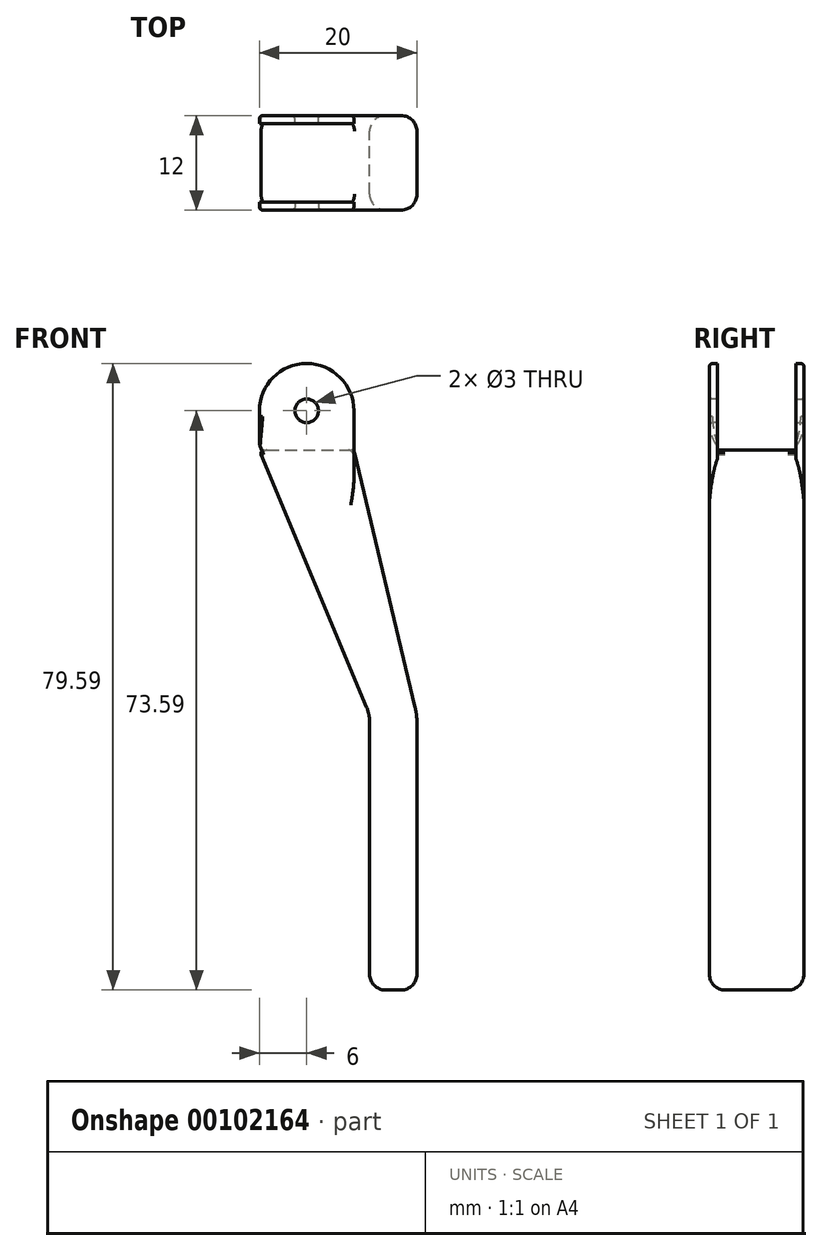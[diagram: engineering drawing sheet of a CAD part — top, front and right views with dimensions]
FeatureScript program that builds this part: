
annotation { "Feature Type Name" : "Feature", "Feature Type Description" : "" }
export const myFeature = defineFeature(function(context is Context, id is Id, definition is map)
    precondition{}
    {
        {
            var Q0;
            Q0=qCreatedBy(makeId("Front.planeOp"),FACE);
            var sketch = newSketch(context, id + "F0", { "sketchPlane" : qUnion([Q0])});
            skLineSegment(sketch, "E0", {"start": v(0, 0) * mm, "end": v(12, 0) * mm});
            skLineSegment(sketch, "E1", {"start": v(12, 0) * mm, "end": v(20, -33.59) * mm});
            skLineSegment(sketch, "E2", {"start": v(20, -33.59) * mm, "end": v(20, -68.59) * mm});
            skLineSegment(sketch, "E3", {"start": v(20, -68.59) * mm, "end": v(14, -68.59) * mm});
            skLineSegment(sketch, "E4", {"start": v(14, -68.59) * mm, "end": v(14, -33.59) * mm});
            skLineSegment(sketch, "E5", {"start": v(14, -33.59) * mm, "end": v(0, 0) * mm});
            skLineSegment(sketch, "E6", {"start": v(14, -33.59) * mm, "end": v(20, -33.59) * mm});
            skSolve(sketch);
        }
        {
            var Q0;
            Q0 = qSketchRegion(id + "F0", true);
            extrude(context, id + "F1", {"entities" : qUnion([Q0]), "depth" : 6 * mm, "hasSecondDirection" : true, "secondDirectionOppositeDirection" : true, "secondDirectionDepth" : 6 * mm});
        }
        {
            var Q0;
            Q0 = qSketchRegion(id + "F0", true);
            extrude(context, id + "F2", {"entities" : qUnion([Q0]), "operationType" : NewBodyOperationType.ADD, "depth" : 6 * mm, "hasSecondDirection" : true, "secondDirectionOppositeDirection" : true, "secondDirectionDepth" : 6 * mm});
        }
        {
            var Q0;
            Q0=makeQuery(id+"F1.opExtrude","CAP_FACE",FACE,{"disambiguationData":[OSD([sQuery(id+"F0.wireOp",EDGE,"E0"),sQuery(id+"F0.wireOp",EDGE,"E1"),sQuery(id+"F0.wireOp",EDGE,"E2"),sQuery(id+"F0.wireOp",EDGE,"E3"),sQuery(id+"F0.wireOp",EDGE,"E4"),sQuery(id+"F0.wireOp",EDGE,"E5")])],"isStart":false});
            var sketch = newSketch(context, id + "F3", { "sketchPlane" : qUnion([Q0])});
            skLineSegment(sketch, "E7.bottom", {"start": v(0, 0) * mm, "end": v(12, 0) * mm});
            skLineSegment(sketch, "E7.top", {"start": v(0, 5) * mm, "end": v(12, 5) * mm});
            skLineSegment(sketch, "E7.left", {"start": v(0, 0) * mm, "end": v(0, 5) * mm});
            skLineSegment(sketch, "E7.right", {"start": v(12, 0) * mm, "end": v(12, 5) * mm});
            skArc(sketch, "E8", {"start": v(12, 5) * mm, "mid": v(6, 11) * mm, "end": v(0, 5) * mm});
            skCircle(sketch, "E9", {"center": v(6, 5) * mm, "radius": 1.5 * mm});
            skSolve(sketch);
        }
        {
            var Q0;
            Q0 = qSketchRegion(id + "F3", true);
            extrude(context, id + "F4", {"entities" : qUnion([Q0]), "oppositeDirection" : true, "depth" : 1 * mm});
        }
        {
            var Q0;
            Q0=makeQuery(id+"F4.opExtrude","SWEPT_BODY",BODY,{"disambiguationData":[OSD([sQuery(id+"F3.wireOp",EDGE,"E7.bottom"),sQuery(id+"F3.wireOp",EDGE,"E7.left"),sQuery(id+"F3.wireOp",EDGE,"E7.right"),sQuery(id+"F3.wireOp",EDGE,"E8"),sQuery(id+"F3.wireOp",EDGE,"E9")])]});
            var Q1;
            Q1=qCreatedBy(makeId("Front.planeOp"),FACE);
            mirror(context, id + "F5", {"operationType" : NewBodyOperationType.ADD, "entities" : qUnion([Q0]), "mirrorPlane" : qUnion([Q1])});
        }
        {
            var Q0;
            Q0=makeQuery(id+"F1.opExtrude","SWEPT_EDGE",EDGE,{"disambiguationData":[OSD([sQuery(id+"F0.wireOp",EDGE,"E1"),sQuery(id+"F0.wireOp",EDGE,"E2"),sQuery(id+"F0.wireOp",EDGE,"E6")])]});
            fillet(context, id + "F6", {"entities" : qUnion([Q0]), "radius" : 8 * mm, "tangentPropagation" : true, "allowEdgeOverflow" : false});
        }
        {
            var Q0;
            Q0=makeQuery(id+"F1.opExtrude","SWEPT_EDGE",EDGE,{"disambiguationData":[OSD([sQuery(id+"F0.wireOp",EDGE,"E4"),sQuery(id+"F0.wireOp",EDGE,"E5"),sQuery(id+"F0.wireOp",EDGE,"E6")])]});
            fillet(context, id + "F7", {"entities" : qUnion([Q0]), "radius" : 5 * mm, "tangentPropagation" : true, "allowEdgeOverflow" : false});
        }
        {
            var Q0;
            Q0=makeQuery(id+"F1.opExtrude","CAP_EDGE",EDGE,{"disambiguationData":[OSD([sQuery(id+"F0.wireOp",EDGE,"E1")])],"isStart":false});
            var Q1;
            Q1=makeQuery(id+"F1.opExtrude","CAP_EDGE",EDGE,{"disambiguationData":[OSD([sQuery(id+"F0.wireOp",EDGE,"E1")])],"isStart":true});
            var Q2;
            Q2=makeQuery(id+"F1.opExtrude","CAP_EDGE",EDGE,{"disambiguationData":[OSD([sQuery(id+"F0.wireOp",EDGE,"E5")])],"isStart":false});
            var Q3;
            Q3=makeQuery(id+"F1.opExtrude","CAP_EDGE",EDGE,{"disambiguationData":[OSD([sQuery(id+"F0.wireOp",EDGE,"E5")])],"isStart":true});
            var Q4;
            Q4=makeQuery(id+"F1.opExtrude","SWEPT_EDGE",EDGE,{"disambiguationData":[OSD([sQuery(id+"F0.wireOp",EDGE,"E3"),sQuery(id+"F0.wireOp",EDGE,"E4")])]});
            var Q5;
            Q5=makeQuery(id+"F1.opExtrude","SWEPT_EDGE",EDGE,{"disambiguationData":[OSD([sQuery(id+"F0.wireOp",EDGE,"E2"),sQuery(id+"F0.wireOp",EDGE,"E3")])]});
            var Q6;
            Q6=makeQuery(id+"F1.opExtrude","CAP_EDGE",EDGE,{"disambiguationData":[OSD([sQuery(id+"F0.wireOp",EDGE,"E3")])],"isStart":false});
            var Q7;
            Q7=makeQuery(id+"F1.opExtrude","CAP_EDGE",EDGE,{"disambiguationData":[OSD([sQuery(id+"F0.wireOp",EDGE,"E3")])],"isStart":true});
            fillet(context, id + "F8", {"entities" : qUnion([Q0, Q1, Q2, Q3, Q4, Q5, Q6, Q7]), "radius" : 2 * mm, "tangentPropagation" : true, "allowEdgeOverflow" : false});
        }
        {
            var Q0;
            Q0=makeQuery(id+"F4.opExtrude","CAP_EDGE",EDGE,{"disambiguationData":[OSD([sQuery(id+"F3.wireOp",EDGE,"E9")])],"isStart":true});
            var Q1;
            Q1=makeQuery(id+"F5.opPattern","COPY",EDGE,{"derivedFrom":makeQuery(id+"F4.opExtrude","CAP_EDGE",EDGE,{"disambiguationData":[OSD([sQuery(id+"F3.wireOp",EDGE,"E9")])],"isStart":true}),"instanceName":"1"});
            var Q2;
            Q2=makeQuery(id+"F5.opPattern","COPY",EDGE,{"derivedFrom":makeQuery(id+"F4.opExtrude","CAP_EDGE",EDGE,{"disambiguationData":[OSD([sQuery(id+"F3.wireOp",EDGE,"E8")])],"isStart":true}),"instanceName":"1"});
            var Q3;
            Q3=makeQuery(id+"F4.opExtrude","CAP_EDGE",EDGE,{"disambiguationData":[OSD([sQuery(id+"F3.wireOp",EDGE,"E8")])],"isStart":true});
            var Q4;
            Q4=makeQuery(id+"F5.boolean.opBoolean","SPLIT",EDGE,{"derivedFrom":makeQuery(id+"F1.opExtrude","SWEPT_EDGE",EDGE,{"disambiguationData":[OSD([sQuery(id+"F0.wireOp",EDGE,"E0"),sQuery(id+"F0.wireOp",EDGE,"E1")])]})});
            var Q5;
            Q5=makeQuery(id+"F5.boolean.opBoolean","SPLIT",EDGE,{"derivedFrom":makeQuery(id+"F1.opExtrude","SWEPT_EDGE",EDGE,{"disambiguationData":[OSD([sQuery(id+"F0.wireOp",EDGE,"E0"),sQuery(id+"F0.wireOp",EDGE,"E5")])]})});
            fillet(context, id + "F9", {"entities" : qUnion([Q0, Q1, Q2, Q3, Q4, Q5]), "radius" : 0.4 * mm, "tangentPropagation" : true, "allowEdgeOverflow" : false});
        }
    });
